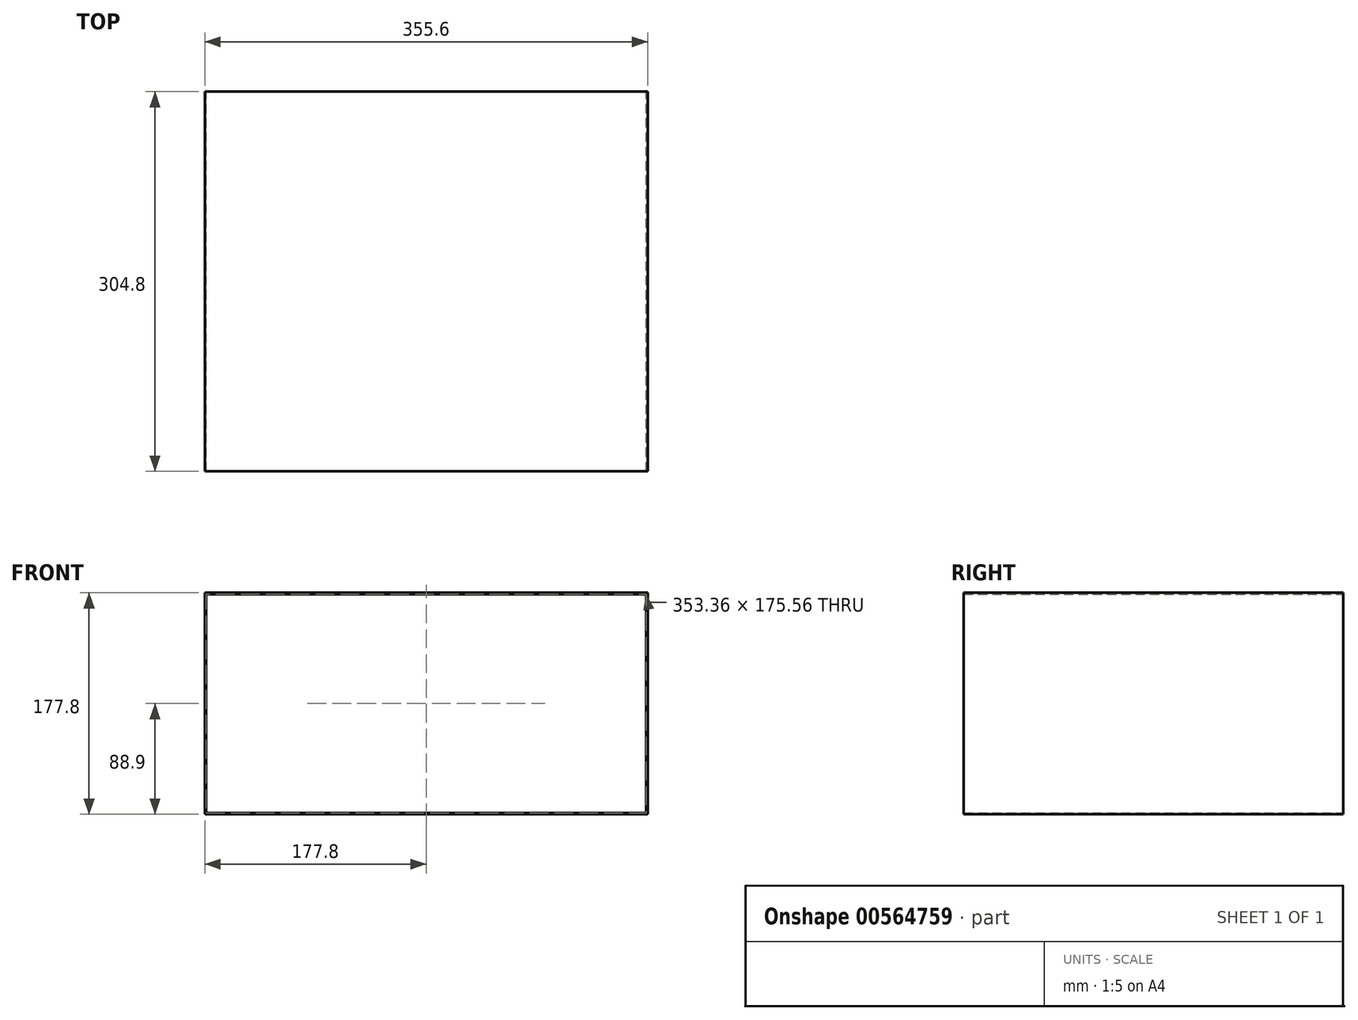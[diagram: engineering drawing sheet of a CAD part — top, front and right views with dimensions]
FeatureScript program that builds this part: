
annotation { "Feature Type Name" : "Feature", "Feature Type Description" : "" }
export const myFeature = defineFeature(function(context is Context, id is Id, definition is map)
    precondition{}
    {
        {
            var Q0;
            Q0=qCreatedBy(makeId("Front.planeOp"),FACE);
            var sketch = newSketch(context, id + "F0", { "sketchPlane" : qUnion([Q0])});
            skLineSegment(sketch, "E0.bottom", {"start": v(-177.8, 88.9) * mm, "end": v(177.8, 88.9) * mm});
            skLineSegment(sketch, "E0.top", {"start": v(-177.8, -88.9) * mm, "end": v(177.8, -88.9) * mm});
            skLineSegment(sketch, "E0.left", {"start": v(-177.8, 88.9) * mm, "end": v(-177.8, -88.9) * mm});
            skLineSegment(sketch, "E0.right", {"start": v(177.8, 88.9) * mm, "end": v(177.8, -88.9) * mm});
            skLineSegment(sketch, "E1.0", {"start": v(-176.68, 87.78) * mm, "end": v(176.68, 87.78) * mm});
            skLineSegment(sketch, "E1.1", {"start": v(-176.68, 87.78) * mm, "end": v(-176.68, -87.78) * mm});
            skLineSegment(sketch, "E1.2", {"start": v(-176.68, -87.78) * mm, "end": v(176.68, -87.78) * mm});
            skLineSegment(sketch, "E1.3", {"start": v(176.68, 87.78) * mm, "end": v(176.68, -87.78) * mm});
            skSolve(sketch);
        }
        {
            var Q0;
            Q0=makeQuery(id+"F0.imprint","IMPRINT",FACE,{"disambiguationData":[TD([[makeQuery(id+"F0.imprint","IMPRINT",EDGE,{"derivedFrom":sQuery(id+"F0.wireOp",EDGE,"E0.bottom")}),-1.0]])]});
            extrude(context, id + "F1", {"entities" : qUnion([Q0]), "depth" : 304.8 * mm, "offsetDistance" : 25.4 * mm});
        }
    });
